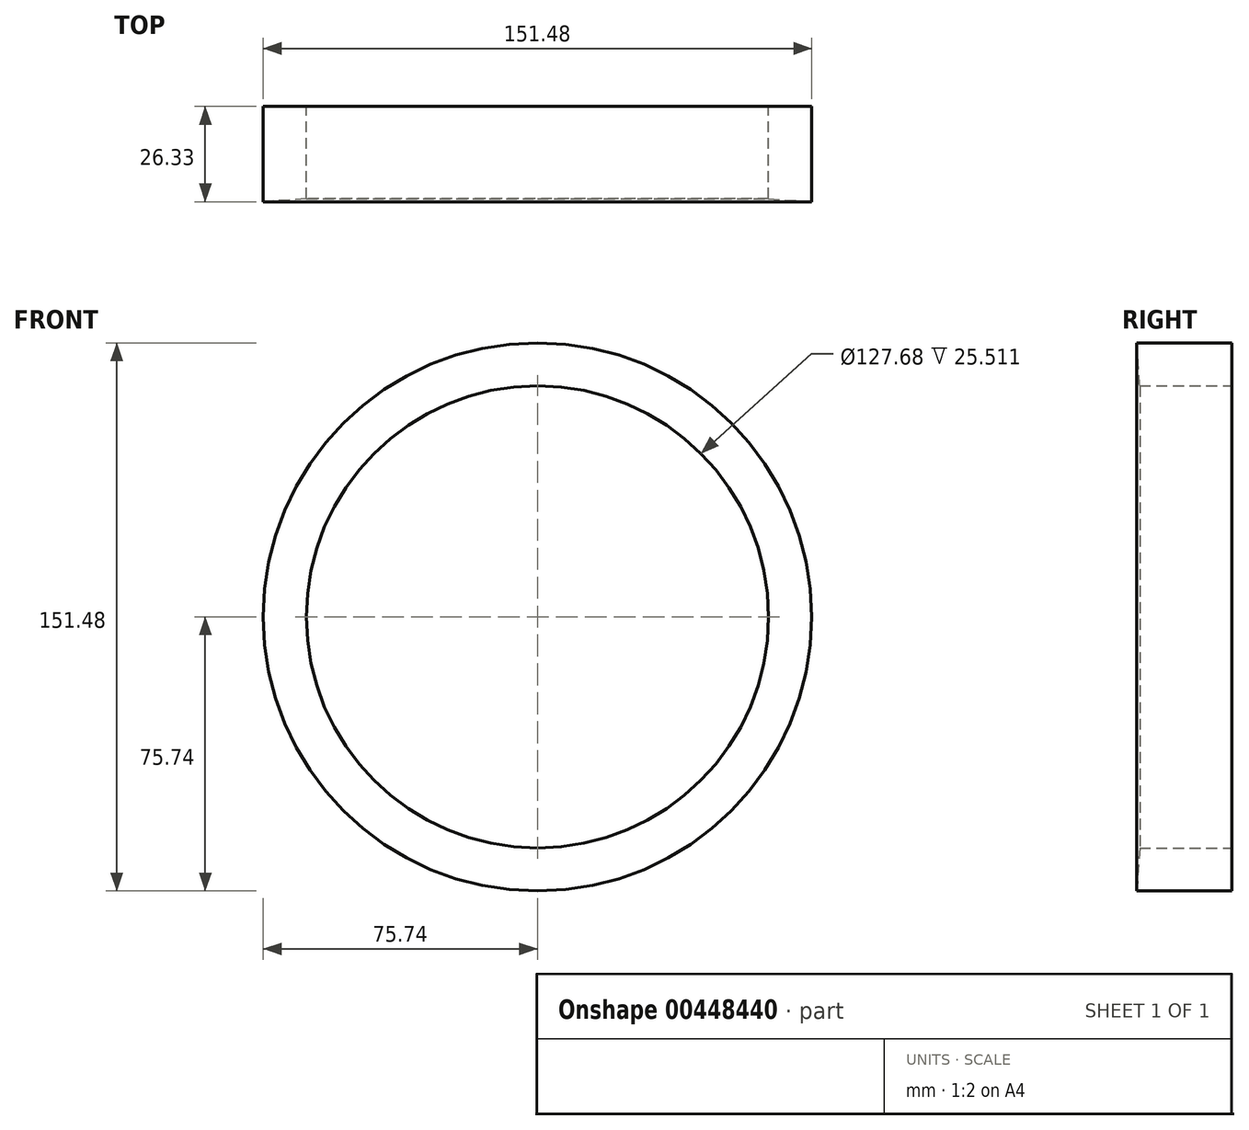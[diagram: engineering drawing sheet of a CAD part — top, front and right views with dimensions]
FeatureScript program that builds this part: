
annotation { "Feature Type Name" : "Feature", "Feature Type Description" : "" }
export const myFeature = defineFeature(function(context is Context, id is Id, definition is map)
    precondition{}
    {
        {
            var Q0;
            Q0=qCreatedBy(makeId("Front.planeOp"),FACE);
            var sketch = newSketch(context, id + "F0", { "sketchPlane" : qUnion([Q0])});
            skCircle(sketch, "E0", {"center": v(0, 0) * mm, "radius": 63.66 * mm});
            skSolve(sketch);
        }
        {
            var Q0;
            Q0 = qSketchRegion(id + "F0", true);
            var sketch = newSketch(context, id + "F1", { "sketchPlane" : qUnion([Q0])});
            skCircle(sketch, "E1", {"center": v(0, 0) * mm, "radius": 55.41 * mm});
            skSolve(sketch);
        }
        {
            var Q0;
            Q0=sQuery(id+"F1.wireOp",EDGE,"E1");
            var Q1;
            Q1=sQuery(id+"F0.wireOp",EDGE,"E0");
            extrude(context, id + "F2", {"bodyType" : ToolBodyType.SURFACE, "surfaceEntities" : qUnion([Q0, Q1]), "depth" : 25.4 * mm});
        }
        {
            var Q0;
            Q0=makeQuery(id+"F2.opExtrude","SWEPT_BODY",BODY,{"disambiguationData":[OSD([sQuery(id+"F1.wireOp",EDGE,"E1")])]});
            deleteBodies(context, id + "F3", {"entities" : qUnion([Q0])});
        }
        {
            var Q0;
            Q0=qCreatedBy(makeId("Right.planeOp"),FACE);
            var sketch = newSketch(context, id + "F4", { "sketchPlane" : qUnion([Q0])});
            skLineSegment(sketch, "E2", {"start": v(-25.51, 63.84) * mm, "end": v(0, 63.84) * mm});
            skLineSegment(sketch, "E3", {"start": v(0, 63.84) * mm, "end": v(0, 75.74) * mm});
            skLineSegment(sketch, "E4", {"start": v(0, 75.74) * mm, "end": v(-26.33, 75.74) * mm});
            skLineSegment(sketch, "E5", {"start": v(-26.33, 75.74) * mm, "end": v(-25.51, 63.84) * mm});
            skSolve(sketch);
        }
        {
            var Q0;
            Q0=makeQuery(id+"F4.imprint","IMPRINT",FACE,{"disambiguationData":[TD([[makeQuery(id+"F4.imprint","IMPRINT",EDGE,{"derivedFrom":sQuery(id+"F4.wireOp",EDGE,"E2")}),1.0]])]});
            var Q1;
            Q1=makeQuery(id+"F2.opExtrude","SWEPT_FACE",FACE,{"disambiguationData":[OSD([sQuery(id+"F0.wireOp",EDGE,"E0")])]});
            revolve(context, id + "F5", {"entities" : qUnion([Q0]), "axis" : qUnion([Q1]), "revolveType" : RevolveType.FULL});
        }
        {
            var Q0;
            Q0=qCreatedBy(makeId("Front.planeOp"),FACE);
            var sketch = newSketch(context, id + "F6", { "sketchPlane" : qUnion([Q0])});
            skText(sketch, "E6", { "text": "WHY", "fontName": "OpenSans-Regular.ttf"});
            const initialGuessF6  = {"E6": [-0.0129, 0.0649, 1, 0, 0.00873]};
            skSetInitialGuess(sketch, initialGuessF6);
            skSolve(sketch);
        }
        {
            var Q0;
            Q0 = qSketchRegion(id + "F6", true);
            var Q1;
            Q1=makeQuery(id+"F5.opRevolve","SWEPT_FACE",FACE,{"disambiguationData":[OSD([sQuery(id+"F4.wireOp",EDGE,"E3")])]});
            extrude(context, id + "F7", {"entities" : qUnion([Q0, Q1]), "operationType" : NewBodyOperationType.ADD, "depth" : 25 * mm});
        }
    });
